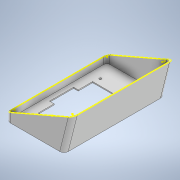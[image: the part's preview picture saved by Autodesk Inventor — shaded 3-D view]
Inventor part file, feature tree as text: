
AUTODESK INVENTOR PART (.ipt)
format: ipt  version: 2022 (Build 260153000, 153)  size: 252,928 bytes
history: native  units: mm
features: sketch x7, extrude x6, projected_geometry x2, fillet x1, plane x1
ambient origin geometry x8: Origin, YZ Plane, XZ Plane, XY Plane, X Axis, Y Axis, Z Axis, Center Point
bodies: Solid1 (feature_tree)
feature tree (17):
  extrude  "Extrusion1"  Depth=193.2mm
  extrude  "Extrusion3"  Depth=4.2mm
  extrude  "Extrusion4"  Depth=65.697mm
  extrude  "Extrusion5"  Depth=4.2mm
  extrude  "Extrusion6"  Depth=126.501mm
  fillet  "Fillet1"  [1 undecoded]
  plane  "Work Plane1"
  extrude  "Extrusion7"  Depth=35.0mm
  sketch  "Sketch10"  dims[d13=8.0mm d14=2.0mm d15=0.0mm d22=105.0mm d23=79.0mm d26=40.0mm d27=40.0mm d29=7.5mm d30=0.0mm d32=12.0mm d33=41.0mm d34=11.0mm d35=79.0mm d36=79.0mm d37=2.0mm d38=60.0mm d39=0.0mm d40=14.0mm d41=0.0mm d42=1000.0mm d43=0.0mm d47=140.0mm d48=193.2mm d49=0.0mm d50=8.0mm d54=90.0deg d55=2.0mm d56=8.0mm d57=193.2mm d58=0.0mm]
  sketch  "Sketch1"  dims[d0=110.94mm d1=193.2mm]
  sketch  "Sketch3"  dims[d2=4.2mm d3=4.2mm]
  sketch  "Sketch4"  dims[d4=65.3mm d5=65.697mm]
  projected_geometry  "Projected Loop2"
  sketch  "Sketch5"  dims[d6=4.2mm d7=4.2mm]
  sketch  "Sketch6"  dims[d8=126.2mm d9=126.501mm d10=0.0mm]
  sketch  "Sketch9"  dims[d11=22.6mm d12=35.0mm]
  projected_geometry  "Projected Loop3"
note: 1 required parameter value undecoded (feature->parameter linkage not recoverable at this tier; creation-order binding heuristic only, values carry confidence <= 0.55)
